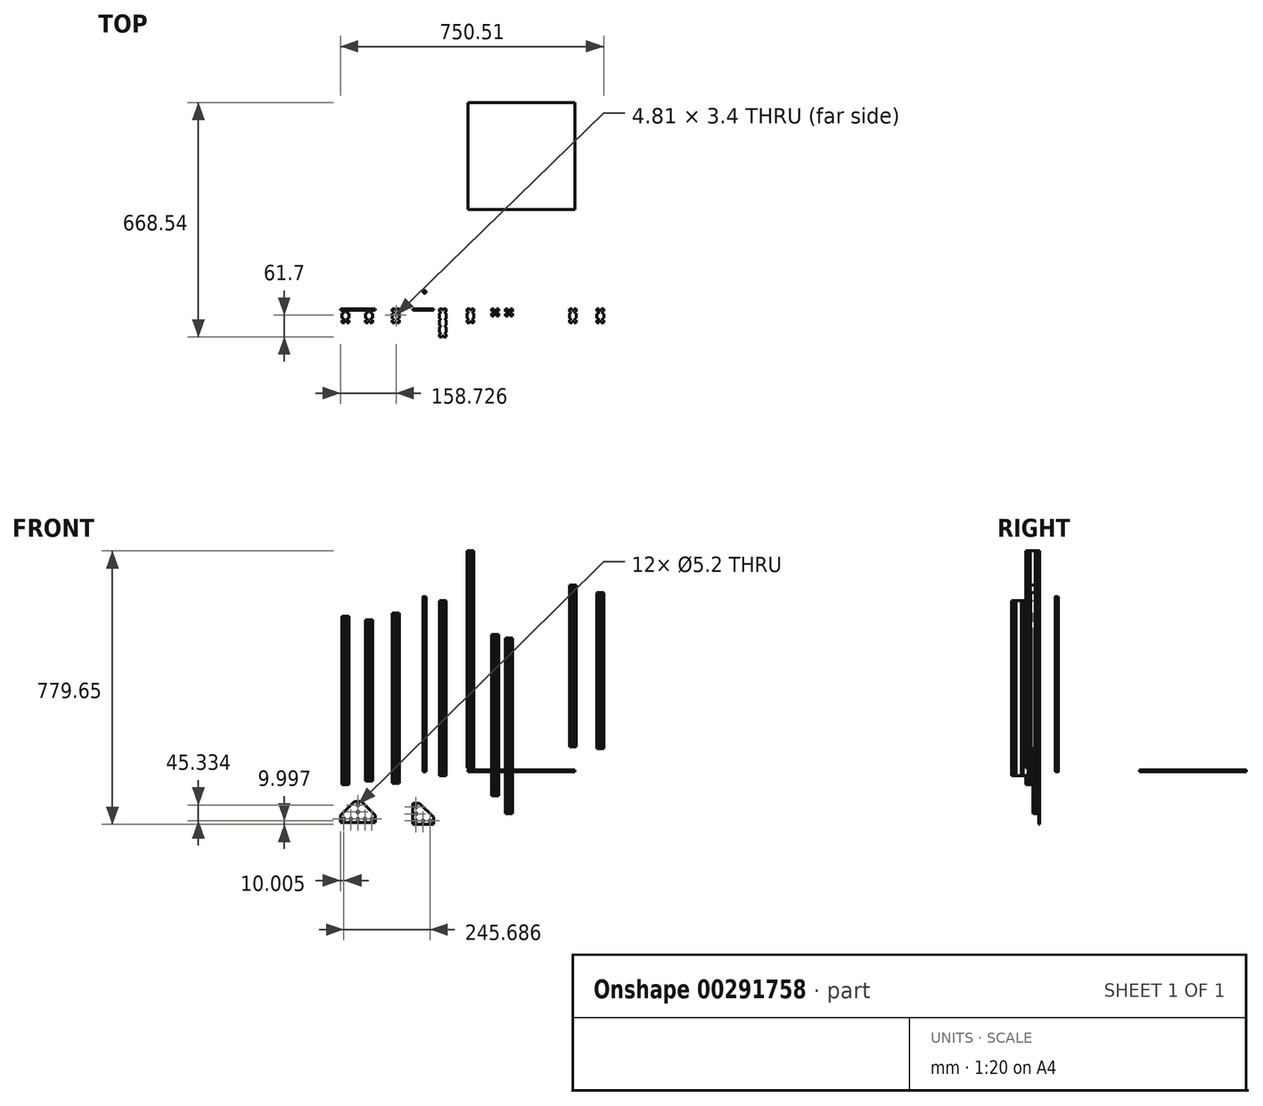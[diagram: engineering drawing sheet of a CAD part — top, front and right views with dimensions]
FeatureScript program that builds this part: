
annotation { "Feature Type Name" : "Feature", "Feature Type Description" : "" }
export const myFeature = defineFeature(function(context is Context, id is Id, definition is map)
    precondition{}
    {
        {
            var Q0;
            Q0=qCreatedBy(makeId("Front.planeOp"),FACE);
            var sketch = newSketch(context, id + "F0", { "sketchPlane" : qUnion([Q0])});
            skLineSegment(sketch, "E0.bottom", {"start": v(-21.8, 488.82) * mm, "end": v(-1.8, 488.82) * mm});
            skLineSegment(sketch, "E0.top", {"start": v(-21.8, -11.18) * mm, "end": v(-1.8, -11.18) * mm});
            skLineSegment(sketch, "E0.left", {"start": v(-21.8, 488.82) * mm, "end": v(-21.8, -11.18) * mm});
            skLineSegment(sketch, "E0.right", {"start": v(-1.8, 488.82) * mm, "end": v(-1.8, -11.18) * mm});
            skSolve(sketch);
        }
        {
            var Q0;
            Q0 = qSketchRegion(id + "F0", true);
            extrude(context, id + "F1", {"entities" : qUnion([Q0]), "depth" : 80 * mm});
        }
        {
            var Q0;
            Q0=qCreatedBy(makeId("Front.planeOp"),FACE);
            var sketch = newSketch(context, id + "F2", { "sketchPlane" : qUnion([Q0])});
            skLineSegment(sketch, "E1.bottom", {"start": v(56.98, 630.24) * mm, "end": v(76.98, 630.24) * mm});
            skLineSegment(sketch, "E1.top", {"start": v(56.98, 10.24) * mm, "end": v(76.98, 10.24) * mm});
            skLineSegment(sketch, "E1.left", {"start": v(56.98, 630.24) * mm, "end": v(56.98, 10.24) * mm});
            skLineSegment(sketch, "E1.right", {"start": v(76.98, 630.24) * mm, "end": v(76.98, 10.24) * mm});
            skSolve(sketch);
        }
        {
            var Q0;
            Q0 = qSketchRegion(id + "F2", true);
            extrude(context, id + "F3", {"entities" : qUnion([Q0]), "depth" : 40 * mm});
        }
        {
            var Q0;
            Q0=qCreatedBy(makeId("Front.planeOp"),FACE);
            var sketch = newSketch(context, id + "F4", { "sketchPlane" : qUnion([Q0])});
            skLineSegment(sketch, "E2.bottom", {"start": v(127.1, 391.51) * mm, "end": v(147.1, 391.51) * mm});
            skLineSegment(sketch, "E2.top", {"start": v(127.1, -68.49) * mm, "end": v(147.1, -68.49) * mm});
            skLineSegment(sketch, "E2.left", {"start": v(127.1, 391.51) * mm, "end": v(127.1, -68.49) * mm});
            skLineSegment(sketch, "E2.right", {"start": v(147.1, 391.51) * mm, "end": v(147.1, -68.49) * mm});
            skSolve(sketch);
        }
        {
            var Q0;
            Q0 = qSketchRegion(id + "F4", true);
            extrude(context, id + "F5", {"entities" : qUnion([Q0]), "depth" : 20 * mm});
        }
        {
            var Q0;
            Q0=qCreatedBy(makeId("Front.planeOp"),FACE);
            var sketch = newSketch(context, id + "F6", { "sketchPlane" : qUnion([Q0])});
            skLineSegment(sketch, "E3.bottom", {"start": v(349.08, 532.32) * mm, "end": v(369.08, 532.32) * mm});
            skLineSegment(sketch, "E3.top", {"start": v(349.08, 72.32) * mm, "end": v(369.08, 72.32) * mm});
            skLineSegment(sketch, "E3.left", {"start": v(349.08, 532.32) * mm, "end": v(349.08, 72.32) * mm});
            skLineSegment(sketch, "E3.right", {"start": v(369.08, 532.32) * mm, "end": v(369.08, 72.32) * mm});
            skSolve(sketch);
        }
        {
            var Q0;
            Q0 = qSketchRegion(id + "F6", true);
            extrude(context, id + "F7", {"entities" : qUnion([Q0]), "depth" : 40 * mm});
        }
        {
            var Q0;
            Q0=qCreatedBy(makeId("Front.planeOp"),FACE);
            var sketch = newSketch(context, id + "F8", { "sketchPlane" : qUnion([Q0])});
            skLineSegment(sketch, "E4.bottom", {"start": v(167.05, 381.28) * mm, "end": v(187.05, 381.28) * mm});
            skLineSegment(sketch, "E4.top", {"start": v(167.05, -118.72) * mm, "end": v(187.05, -118.72) * mm});
            skLineSegment(sketch, "E4.left", {"start": v(167.05, 381.28) * mm, "end": v(167.05, -118.72) * mm});
            skLineSegment(sketch, "E4.right", {"start": v(187.05, 381.28) * mm, "end": v(187.05, -118.72) * mm});
            skSolve(sketch);
        }
        {
            var Q0;
            Q0 = qSketchRegion(id + "F8", true);
            extrude(context, id + "F9", {"entities" : qUnion([Q0]), "depth" : 20 * mm});
        }
        {
            var Q0;
            Q0=qCreatedBy(makeId("Front.planeOp"),FACE);
            var sketch = newSketch(context, id + "F10", { "sketchPlane" : qUnion([Q0])});
            skLineSegment(sketch, "E5.bottom", {"start": v(-298.86, 444.23) * mm, "end": v(-278.86, 444.23) * mm});
            skLineSegment(sketch, "E5.top", {"start": v(-298.86, -35.77) * mm, "end": v(-278.86, -35.77) * mm});
            skLineSegment(sketch, "E5.left", {"start": v(-298.86, 444.23) * mm, "end": v(-298.86, -35.77) * mm});
            skLineSegment(sketch, "E5.right", {"start": v(-278.86, 444.23) * mm, "end": v(-278.86, -35.77) * mm});
            skSolve(sketch);
        }
        {
            var Q0;
            Q0 = qSketchRegion(id + "F10", true);
            extrude(context, id + "F11", {"entities" : qUnion([Q0]), "depth" : 40 * mm});
        }
        {
            var Q0;
            Q0=qCreatedBy(makeId("Front.planeOp"),FACE);
            var sketch = newSketch(context, id + "F12", { "sketchPlane" : qUnion([Q0])});
            skLineSegment(sketch, "E6.bottom", {"start": v(-232.38, 433.39) * mm, "end": v(-212.38, 433.39) * mm});
            skLineSegment(sketch, "E6.top", {"start": v(-232.38, -26.61) * mm, "end": v(-212.38, -26.61) * mm});
            skLineSegment(sketch, "E6.left", {"start": v(-232.38, 433.39) * mm, "end": v(-232.38, -26.61) * mm});
            skLineSegment(sketch, "E6.right", {"start": v(-212.38, 433.39) * mm, "end": v(-212.38, -26.61) * mm});
            skSolve(sketch);
        }
        {
            var Q0;
            Q0 = qSketchRegion(id + "F12", true);
            extrude(context, id + "F13", {"entities" : qUnion([Q0]), "depth" : 40 * mm});
        }
        {
            var Q0;
            Q0=qCreatedBy(makeId("Top.planeOp"),FACE);
            var sketch = newSketch(context, id + "F14", { "sketchPlane" : qUnion([Q0])});
            skCircle(sketch, "E7", {"center": v(-63.8, 48.43) * mm, "radius": 4 * mm});
            skSolve(sketch);
        }
        {
            var Q0;
            Q0 = qSketchRegion(id + "F14", true);
            extrude(context, id + "F15", {"entities" : qUnion([Q0]), "depth" : 500 * mm});
        }
        {
            var Q0;
            Q0=qCreatedBy(makeId("Top.planeOp"),FACE);
            var sketch = newSketch(context, id + "F16", { "sketchPlane" : qUnion([Q0])});
            skLineSegment(sketch, "E8.bottom", {"start": v(59.64, 588.54) * mm, "end": v(364.44, 588.54) * mm});
            skLineSegment(sketch, "E8.top", {"start": v(59.64, 283.74) * mm, "end": v(364.44, 283.74) * mm});
            skLineSegment(sketch, "E8.left", {"start": v(59.64, 588.54) * mm, "end": v(59.64, 283.74) * mm});
            skLineSegment(sketch, "E8.right", {"start": v(364.44, 588.54) * mm, "end": v(364.44, 283.74) * mm});
            skSolve(sketch);
        }
        {
            var Q0;
            Q0 = qSketchRegion(id + "F16", true);
            extrude(context, id + "F17", {"entities" : qUnion([Q0]), "depth" : 6 * mm});
        }
        {
            var Q0;
            Q0=qCreatedBy(makeId("Front.planeOp"),FACE);
            var sketch = newSketch(context, id + "F18", { "sketchPlane" : qUnion([Q0])});
            skLineSegment(sketch, "E9.bottom", {"start": v(-155.45, 452.3) * mm, "end": v(-135.45, 452.3) * mm});
            skLineSegment(sketch, "E9.top", {"start": v(-155.45, -32.7) * mm, "end": v(-135.45, -32.7) * mm});
            skLineSegment(sketch, "E9.left", {"start": v(-155.45, 452.3) * mm, "end": v(-155.45, -32.7) * mm});
            skLineSegment(sketch, "E9.right", {"start": v(-135.45, 452.3) * mm, "end": v(-135.45, -32.7) * mm});
            skSolve(sketch);
        }
        {
            var Q0;
            Q0 = qSketchRegion(id + "F18", true);
            extrude(context, id + "F19", {"entities" : qUnion([Q0]), "depth" : 40 * mm});
        }
        {
            var Q0;
            Q0=qCreatedBy(makeId("Front.planeOp"),FACE);
            var sketch = newSketch(context, id + "F20", { "sketchPlane" : qUnion([Q0])});
            skLineSegment(sketch, "E10.bottom", {"start": v(426.75, 511.38) * mm, "end": v(446.75, 511.38) * mm});
            skLineSegment(sketch, "E10.top", {"start": v(426.75, 66.38) * mm, "end": v(446.75, 66.38) * mm});
            skLineSegment(sketch, "E10.left", {"start": v(426.75, 511.38) * mm, "end": v(426.75, 66.38) * mm});
            skLineSegment(sketch, "E10.right", {"start": v(446.75, 511.38) * mm, "end": v(446.75, 66.38) * mm});
            skSolve(sketch);
        }
        {
            var Q0;
            Q0 = qSketchRegion(id + "F20", true);
            extrude(context, id + "F21", {"entities" : qUnion([Q0]), "depth" : 40 * mm});
        }
        {
            var Q0;
            Q0=makeQuery(id+"F11.opExtrude","SWEPT_FACE",FACE,{"disambiguationData":[OSD([sQuery(id+"F10.wireOp",EDGE,"E5.bottom")])]});
            var sketch = newSketch(context, id + "F22", { "sketchPlane" : qUnion([Q0])});
            skLineSegment(sketch, "E11", {"start": v(-288.86, 0) * mm, "end": v(-288.86, -40) * mm, "construction": true});
            skLineSegment(sketch, "E12", {"start": v(-288.86, -40) * mm, "end": v(-298.86, -20) * mm, "construction": true});
            skLineSegment(sketch, "E13", {"start": v(-298.86, -20) * mm, "end": v(-278.86, 0) * mm, "construction": true});
            skLineSegment(sketch, "E14", {"start": v(-288.86, -10) * mm, "end": v(-283.86, -10) * mm, "construction": true});
            skPoint(sketch, "E15.oppositeSnap0", {"position": v(-283.86, -10) * mm});
            skLineSegment(sketch, "E15.top", {"start": v(-278.86, -6.61) * mm, "end": v(-283.86, -6.61) * mm});
            skLineSegment(sketch, "E15.left", {"start": v(-278.86, -10) * mm, "end": v(-278.86, -6.61) * mm});
            skLineSegment(sketch, "E15.right", {"start": v(-283.86, -10) * mm, "end": v(-283.86, -6.61) * mm});
            skLineSegment(sketch, "E16.MirrorCS", {"start": v(-278.86, -13.39) * mm, "end": v(-283.86, -13.39) * mm});
            skLineSegment(sketch, "E17.MirrorCS", {"start": v(-283.86, -10) * mm, "end": v(-283.86, -13.39) * mm});
            skLineSegment(sketch, "E18.MirrorCS", {"start": v(-278.86, -10) * mm, "end": v(-278.86, -13.39) * mm});
            skLineSegment(sketch, "E19", {"start": v(-298.86, -20) * mm, "end": v(-278.86, -20) * mm, "construction": true});
            skLineSegment(sketch, "E20.MirrorCS", {"start": v(-278.86, -26.61) * mm, "end": v(-283.86, -26.61) * mm});
            skLineSegment(sketch, "E21.MirrorCS", {"start": v(-283.86, -30) * mm, "end": v(-283.86, -26.61) * mm});
            skLineSegment(sketch, "E22.MirrorCS", {"start": v(-283.86, -30) * mm, "end": v(-283.86, -33.39) * mm});
            skLineSegment(sketch, "E23.MirrorCS", {"start": v(-278.86, -33.39) * mm, "end": v(-283.86, -33.39) * mm});
            skLineSegment(sketch, "E24.MirrorCS", {"start": v(-278.86, -30) * mm, "end": v(-278.86, -33.39) * mm});
            skLineSegment(sketch, "E25.MirrorCS", {"start": v(-278.86, -30) * mm, "end": v(-278.86, -26.61) * mm});
            skLineSegment(sketch, "E26.MirrorCS", {"start": v(-298.86, -13.39) * mm, "end": v(-293.86, -13.39) * mm});
            skLineSegment(sketch, "E27.MirrorCS", {"start": v(-298.86, -6.61) * mm, "end": v(-293.86, -6.61) * mm});
            skLineSegment(sketch, "E28.MirrorCS", {"start": v(-293.86, -10) * mm, "end": v(-293.86, -6.61) * mm});
            skLineSegment(sketch, "E29.MirrorCS", {"start": v(-293.86, -10) * mm, "end": v(-293.86, -13.39) * mm});
            skLineSegment(sketch, "E30.MirrorCS", {"start": v(-298.86, -26.61) * mm, "end": v(-293.86, -26.61) * mm});
            skLineSegment(sketch, "E31.MirrorCS", {"start": v(-293.86, -30) * mm, "end": v(-293.86, -26.61) * mm});
            skLineSegment(sketch, "E32.MirrorCS", {"start": v(-298.86, -33.39) * mm, "end": v(-293.86, -33.39) * mm});
            skLineSegment(sketch, "E33.MirrorCS", {"start": v(-293.86, -30) * mm, "end": v(-293.86, -33.39) * mm});
            skLineSegment(sketch, "E34.MirrorCS", {"start": v(-298.86, -30) * mm, "end": v(-298.86, -33.39) * mm});
            skLineSegment(sketch, "E35.MirrorCS", {"start": v(-298.86, -30) * mm, "end": v(-298.86, -26.61) * mm});
            skLineSegment(sketch, "E36.MirrorCS", {"start": v(-298.86, -10) * mm, "end": v(-298.86, -13.39) * mm});
            skLineSegment(sketch, "E37.MirrorCS", {"start": v(-298.86, -10) * mm, "end": v(-298.86, -6.61) * mm});
            skLineSegment(sketch, "E38.MirrorCS", {"start": v(-285.47, 0) * mm, "end": v(-285.47, -5) * mm});
            skLineSegment(sketch, "E39.MirrorCS", {"start": v(-292.25, 0) * mm, "end": v(-292.25, -5) * mm});
            skLineSegment(sketch, "E40.MirrorCS", {"start": v(-288.86, -5) * mm, "end": v(-285.47, -5) * mm});
            skLineSegment(sketch, "E41.MirrorCS", {"start": v(-288.86, -5) * mm, "end": v(-292.25, -5) * mm});
            skLineSegment(sketch, "E42.MirrorCS", {"start": v(-288.86, 0) * mm, "end": v(-292.25, 0) * mm});
            skLineSegment(sketch, "E43.MirrorCS", {"start": v(-288.86, 0) * mm, "end": v(-285.47, 0) * mm});
            skLineSegment(sketch, "E44.MirrorCS", {"start": v(-288.86, -35) * mm, "end": v(-292.25, -35) * mm});
            skLineSegment(sketch, "E45.MirrorCS", {"start": v(-292.25, -40) * mm, "end": v(-292.25, -35) * mm});
            skLineSegment(sketch, "E46.MirrorCS", {"start": v(-285.47, -40) * mm, "end": v(-285.47, -35) * mm});
            skLineSegment(sketch, "E47.MirrorCS", {"start": v(-288.86, -35) * mm, "end": v(-285.47, -35) * mm});
            skLineSegment(sketch, "E48.MirrorCS", {"start": v(-288.86, -40) * mm, "end": v(-285.47, -40) * mm});
            skLineSegment(sketch, "E49.MirrorCS", {"start": v(-288.86, -40) * mm, "end": v(-292.25, -40) * mm});
            skSolve(sketch);
        }
        {
            var Q0;
            Q0 = qSketchRegion(id + "F22", true);
            extrude(context, id + "F23", {"entities" : qUnion([Q0]), "operationType" : NewBodyOperationType.REMOVE, "oppositeDirection" : true, "depth" : 900 * mm});
        }
        {
            var Q0;
            Q0=makeQuery(id+"F1.opExtrude","SWEPT_FACE",FACE,{"disambiguationData":[OSD([sQuery(id+"F0.wireOp",EDGE,"E0.bottom")])]});
            var sketch = newSketch(context, id + "F24", { "sketchPlane" : qUnion([Q0])});
            skLineSegment(sketch, "E50", {"start": v(-21.8, -40) * mm, "end": v(-1.8, -40) * mm, "construction": true});
            skLineSegment(sketch, "E51", {"start": v(-1.8, -40) * mm, "end": v(-11.8, 0) * mm, "construction": true});
            skLineSegment(sketch, "E52", {"start": v(-11.8, 0) * mm, "end": v(-11.8, -80) * mm, "construction": true});
            skLineSegment(sketch, "E53", {"start": v(-21.8, -80) * mm, "end": v(-1.8, -40) * mm, "construction": true});
            skLineSegment(sketch, "E54", {"start": v(-21.8, -40) * mm, "end": v(-1.8, 0) * mm, "construction": true});
            skLineSegment(sketch, "E55", {"start": v(-11.8, -20) * mm, "end": v(-1.8, -20) * mm, "construction": true});
            skLineSegment(sketch, "E56", {"start": v(-11.8, -20) * mm, "end": v(-1.8, -40) * mm, "construction": true});
            skLineSegment(sketch, "E57", {"start": v(-11.8, -40) * mm, "end": v(-1.8, -20) * mm, "construction": true});
            skLineSegment(sketch, "E58", {"start": v(-6.8, -30) * mm, "end": v(-1.8, -30) * mm, "construction": true});
            skLineSegment(sketch, "E59.bottom", {"start": v(-4.87, -27.72) * mm, "end": v(-1.8, -27.72) * mm});
            skLineSegment(sketch, "E59.top", {"start": v(-4.87, -32.4) * mm, "end": v(-1.8, -32.4) * mm});
            skLineSegment(sketch, "E59.left", {"start": v(-4.87, -27.72) * mm, "end": v(-4.87, -32.4) * mm});
            skLineSegment(sketch, "E59.right", {"start": v(-1.8, -27.72) * mm, "end": v(-1.8, -32.4) * mm});
            skLineSegment(sketch, "E60.MirrorCS", {"start": v(-4.87, -12.28) * mm, "end": v(-1.8, -12.28) * mm});
            skLineSegment(sketch, "E61.MirrorCS", {"start": v(-4.87, -12.28) * mm, "end": v(-4.87, -7.6) * mm});
            skLineSegment(sketch, "E62.MirrorCS", {"start": v(-4.87, -7.6) * mm, "end": v(-1.8, -7.6) * mm});
            skLineSegment(sketch, "E63.MirrorCS", {"start": v(-1.8, -12.28) * mm, "end": v(-1.8, -7.6) * mm});
            skLineSegment(sketch, "E64.MirrorCS", {"start": v(-18.73, -12.28) * mm, "end": v(-21.8, -12.28) * mm});
            skLineSegment(sketch, "E65.MirrorCS", {"start": v(-18.73, -12.28) * mm, "end": v(-18.73, -7.6) * mm});
            skLineSegment(sketch, "E66.MirrorCS", {"start": v(-18.73, -7.6) * mm, "end": v(-21.8, -7.6) * mm});
            skLineSegment(sketch, "E67.MirrorCS", {"start": v(-21.8, -12.28) * mm, "end": v(-21.8, -7.6) * mm});
            skLineSegment(sketch, "E68.MirrorCS", {"start": v(-18.73, -27.72) * mm, "end": v(-21.8, -27.72) * mm});
            skLineSegment(sketch, "E69.MirrorCS", {"start": v(-18.73, -27.72) * mm, "end": v(-18.73, -32.4) * mm});
            skLineSegment(sketch, "E70.MirrorCS", {"start": v(-21.8, -40) * mm, "end": v(-11.8, 0) * mm, "construction": true});
            skLineSegment(sketch, "E71.MirrorCS", {"start": v(-18.73, -32.4) * mm, "end": v(-21.8, -32.4) * mm});
            skLineSegment(sketch, "E72.MirrorCS", {"start": v(-21.8, -27.72) * mm, "end": v(-21.8, -32.4) * mm});
            skLineSegment(sketch, "E73.bottom", {"start": v(-14.19, 0) * mm, "end": v(-9.32, 0) * mm});
            skLineSegment(sketch, "E73.top", {"start": v(-14.19, -3.05) * mm, "end": v(-9.32, -3.05) * mm});
            skLineSegment(sketch, "E73.left", {"start": v(-14.19, 0) * mm, "end": v(-14.19, -3.05) * mm});
            skLineSegment(sketch, "E73.right", {"start": v(-9.32, 0) * mm, "end": v(-9.32, -3.05) * mm});
            skLineSegment(sketch, "E74.MirrorCS", {"start": v(-14.19, -80) * mm, "end": v(-9.32, -80) * mm});
            skLineSegment(sketch, "E75.MirrorCS", {"start": v(-1.8, -52.28) * mm, "end": v(-1.8, -47.6) * mm});
            skLineSegment(sketch, "E76.MirrorCS", {"start": v(-18.73, -67.72) * mm, "end": v(-21.8, -67.72) * mm});
            skLineSegment(sketch, "E77.MirrorCS", {"start": v(-18.73, -67.72) * mm, "end": v(-18.73, -72.4) * mm});
            skLineSegment(sketch, "E78.MirrorCS", {"start": v(-4.87, -52.28) * mm, "end": v(-4.87, -47.6) * mm});
            skLineSegment(sketch, "E79.MirrorCS", {"start": v(-14.19, -76.95) * mm, "end": v(-9.32, -76.95) * mm});
            skLineSegment(sketch, "E80.MirrorCS", {"start": v(-4.87, -52.28) * mm, "end": v(-1.8, -52.28) * mm});
            skLineSegment(sketch, "E81.MirrorCS", {"start": v(-14.19, -80) * mm, "end": v(-14.19, -76.95) * mm});
            skLineSegment(sketch, "E82.MirrorCS", {"start": v(-1.8, -67.72) * mm, "end": v(-1.8, -72.4) * mm});
            skLineSegment(sketch, "E83.MirrorCS", {"start": v(-9.32, -80) * mm, "end": v(-9.32, -76.95) * mm});
            skLineSegment(sketch, "E84.MirrorCS", {"start": v(-18.73, -47.6) * mm, "end": v(-21.8, -47.6) * mm});
            skLineSegment(sketch, "E85.MirrorCS", {"start": v(-4.87, -67.72) * mm, "end": v(-4.87, -72.4) * mm});
            skLineSegment(sketch, "E86.MirrorCS", {"start": v(-4.87, -47.6) * mm, "end": v(-1.8, -47.6) * mm});
            skLineSegment(sketch, "E87.MirrorCS", {"start": v(-18.73, -72.4) * mm, "end": v(-21.8, -72.4) * mm});
            skLineSegment(sketch, "E88.MirrorCS", {"start": v(-11.8, -60) * mm, "end": v(-1.8, -60) * mm, "construction": true});
            skLineSegment(sketch, "E89.MirrorCS", {"start": v(-6.8, -50) * mm, "end": v(-1.8, -50) * mm, "construction": true});
            skLineSegment(sketch, "E90.MirrorCS", {"start": v(-21.8, -67.72) * mm, "end": v(-21.8, -72.4) * mm});
            skLineSegment(sketch, "E91.MirrorCS", {"start": v(-18.73, -52.28) * mm, "end": v(-21.8, -52.28) * mm});
            skLineSegment(sketch, "E92.MirrorCS", {"start": v(-21.8, -52.28) * mm, "end": v(-21.8, -47.6) * mm});
            skLineSegment(sketch, "E93.MirrorCS", {"start": v(-4.87, -72.4) * mm, "end": v(-1.8, -72.4) * mm});
            skLineSegment(sketch, "E94.MirrorCS", {"start": v(-18.73, -52.28) * mm, "end": v(-18.73, -47.6) * mm});
            skLineSegment(sketch, "E95.MirrorCS", {"start": v(-4.87, -67.72) * mm, "end": v(-1.8, -67.72) * mm});
            skSolve(sketch);
        }
        {
            var Q0;
            Q0 = qSketchRegion(id + "F24", true);
            extrude(context, id + "F25", {"entities" : qUnion([Q0]), "operationType" : NewBodyOperationType.REMOVE, "oppositeDirection" : true, "depth" : 999 * mm});
        }
        {
            var Q0;
            Q0=makeQuery(id+"F3.opExtrude","SWEPT_FACE",FACE,{"disambiguationData":[OSD([sQuery(id+"F2.wireOp",EDGE,"E1.bottom")])]});
            var sketch = newSketch(context, id + "F26", { "sketchPlane" : qUnion([Q0])});
            skLineSegment(sketch, "E96", {"start": v(66.98, 0) * mm, "end": v(66.98, -40) * mm, "construction": true});
            skLineSegment(sketch, "E97", {"start": v(56.98, -20) * mm, "end": v(76.98, -20) * mm, "construction": true});
            skLineSegment(sketch, "E98", {"start": v(76.98, -20) * mm, "end": v(56.98, 0) * mm, "construction": true});
            skLineSegment(sketch, "E99", {"start": v(66.98, -10) * mm, "end": v(76.98, -10) * mm, "construction": true});
            skLineSegment(sketch, "E100.bottom", {"start": v(76.98, -7.44) * mm, "end": v(73.45, -7.44) * mm});
            skLineSegment(sketch, "E100.top", {"start": v(76.98, -12.74) * mm, "end": v(73.45, -12.74) * mm});
            skLineSegment(sketch, "E100.left", {"start": v(76.98, -7.44) * mm, "end": v(76.98, -12.74) * mm});
            skLineSegment(sketch, "E100.right", {"start": v(73.45, -7.44) * mm, "end": v(73.45, -12.74) * mm});
            skLineSegment(sketch, "E101.bottom", {"start": v(64.57, 0) * mm, "end": v(69.67, 0) * mm});
            skLineSegment(sketch, "E101.top", {"start": v(64.57, -3.15) * mm, "end": v(69.67, -3.15) * mm});
            skLineSegment(sketch, "E101.left", {"start": v(64.57, 0) * mm, "end": v(64.57, -3.15) * mm});
            skLineSegment(sketch, "E101.right", {"start": v(69.67, 0) * mm, "end": v(69.67, -3.15) * mm});
            skLineSegment(sketch, "E102.MirrorCS", {"start": v(56.98, -12.74) * mm, "end": v(60.52, -12.74) * mm});
            skLineSegment(sketch, "E103.MirrorCS", {"start": v(56.98, -7.44) * mm, "end": v(60.52, -7.44) * mm});
            skLineSegment(sketch, "E104.MirrorCS", {"start": v(60.52, -7.44) * mm, "end": v(60.52, -12.74) * mm});
            skLineSegment(sketch, "E105.MirrorCS", {"start": v(56.98, -7.44) * mm, "end": v(56.98, -12.74) * mm});
            skLineSegment(sketch, "E106.MirrorCS", {"start": v(56.98, -7.26) * mm, "end": v(60.52, -7.26) * mm});
            skLineSegment(sketch, "E107.MirrorCS", {"start": v(56.98, -12.56) * mm, "end": v(60.52, -12.56) * mm});
            skLineSegment(sketch, "E108.MirrorCS", {"start": v(60.52, -12.56) * mm, "end": v(60.52, -7.26) * mm});
            skLineSegment(sketch, "E109.MirrorCS", {"start": v(56.98, -12.56) * mm, "end": v(56.98, -7.26) * mm});
            skLineSegment(sketch, "E110.MirrorCS", {"start": v(76.98, -12.56) * mm, "end": v(73.45, -12.56) * mm});
            skLineSegment(sketch, "E111.MirrorCS", {"start": v(73.45, -12.56) * mm, "end": v(73.45, -7.26) * mm});
            skLineSegment(sketch, "E112.MirrorCS", {"start": v(76.98, -7.26) * mm, "end": v(73.45, -7.26) * mm});
            skLineSegment(sketch, "E113.MirrorCS", {"start": v(76.98, -12.56) * mm, "end": v(76.98, -7.26) * mm});
            skLineSegment(sketch, "E114.MirrorCS", {"start": v(56.98, 0) * mm, "end": v(76.98, 0) * mm, "construction": true});
            skLineSegment(sketch, "E115.MirrorCS", {"start": v(76.98, 0) * mm, "end": v(56.98, -20) * mm, "construction": true});
            skLineSegment(sketch, "E116.MirrorCS", {"start": v(76.98, -27.44) * mm, "end": v(76.98, -32.74) * mm});
            skLineSegment(sketch, "E117.MirrorCS", {"start": v(56.98, -32.56) * mm, "end": v(56.98, -27.26) * mm});
            skLineSegment(sketch, "E118.MirrorCS", {"start": v(76.98, -32.56) * mm, "end": v(76.98, -27.26) * mm});
            skLineSegment(sketch, "E119.MirrorCS", {"start": v(73.45, -27.44) * mm, "end": v(73.45, -32.74) * mm});
            skLineSegment(sketch, "E120.MirrorCS", {"start": v(60.52, -32.56) * mm, "end": v(60.52, -27.26) * mm});
            skLineSegment(sketch, "E121.MirrorCS", {"start": v(56.98, -27.44) * mm, "end": v(56.98, -32.74) * mm});
            skLineSegment(sketch, "E122.MirrorCS", {"start": v(64.57, -40) * mm, "end": v(69.67, -40) * mm});
            skLineSegment(sketch, "E123.MirrorCS", {"start": v(73.45, -32.56) * mm, "end": v(73.45, -27.26) * mm});
            skLineSegment(sketch, "E124.MirrorCS", {"start": v(60.52, -27.44) * mm, "end": v(60.52, -32.74) * mm});
            skLineSegment(sketch, "E125.MirrorCS", {"start": v(76.98, -32.74) * mm, "end": v(73.45, -32.74) * mm});
            skLineSegment(sketch, "E126.MirrorCS", {"start": v(56.98, -32.74) * mm, "end": v(60.52, -32.74) * mm});
            skLineSegment(sketch, "E127.MirrorCS", {"start": v(56.98, -27.44) * mm, "end": v(60.52, -27.44) * mm});
            skLineSegment(sketch, "E128.MirrorCS", {"start": v(64.57, -40) * mm, "end": v(64.57, -36.85) * mm});
            skLineSegment(sketch, "E129.MirrorCS", {"start": v(69.67, -40) * mm, "end": v(69.67, -36.85) * mm});
            skLineSegment(sketch, "E130.MirrorCS", {"start": v(56.98, -27.26) * mm, "end": v(60.52, -27.26) * mm});
            skLineSegment(sketch, "E131.MirrorCS", {"start": v(76.98, -32.56) * mm, "end": v(73.45, -32.56) * mm});
            skLineSegment(sketch, "E132.MirrorCS", {"start": v(76.98, -27.44) * mm, "end": v(73.45, -27.44) * mm});
            skLineSegment(sketch, "E133.MirrorCS", {"start": v(56.98, -32.56) * mm, "end": v(60.52, -32.56) * mm});
            skLineSegment(sketch, "E134.MirrorCS", {"start": v(76.98, -27.26) * mm, "end": v(73.45, -27.26) * mm});
            skLineSegment(sketch, "E135.MirrorCS", {"start": v(64.57, -36.85) * mm, "end": v(69.67, -36.85) * mm});
            skLineSegment(sketch, "E136.MirrorCS", {"start": v(56.98, -40) * mm, "end": v(76.98, -40) * mm, "construction": true});
            skLineSegment(sketch, "E137.MirrorCS", {"start": v(66.98, -30) * mm, "end": v(76.98, -30) * mm, "construction": true});
            skSolve(sketch);
        }
        {
            var Q0;
            Q0 = qSketchRegion(id + "F26", true);
            extrude(context, id + "F27", {"entities" : qUnion([Q0]), "operationType" : NewBodyOperationType.REMOVE, "oppositeDirection" : true, "depth" : 999 * mm});
        }
        {
            var Q0;
            Q0=makeQuery(id+"F19.opExtrude","SWEPT_FACE",FACE,{"disambiguationData":[OSD([sQuery(id+"F18.wireOp",EDGE,"E9.bottom")])]});
            var sketch = newSketch(context, id + "F28", { "sketchPlane" : qUnion([Q0])});
            skLineSegment(sketch, "E138", {"start": v(-155.45, -20) * mm, "end": v(-135.45, -20) * mm, "construction": true});
            skLineSegment(sketch, "E139", {"start": v(-135.45, -20) * mm, "end": v(-155.45, 0) * mm, "construction": true});
            skLineSegment(sketch, "E140.bottom", {"start": v(-147.9, 0) * mm, "end": v(-142.97, 0) * mm});
            skLineSegment(sketch, "E140.top", {"start": v(-147.9, -2.85) * mm, "end": v(-142.97, -2.85) * mm});
            skLineSegment(sketch, "E140.left", {"start": v(-147.9, 0) * mm, "end": v(-147.9, -2.85) * mm});
            skLineSegment(sketch, "E140.right", {"start": v(-142.97, 0) * mm, "end": v(-142.97, -2.85) * mm});
            skLineSegment(sketch, "E141.bottom", {"start": v(-135.45, -8) * mm, "end": v(-138.85, -8) * mm});
            skLineSegment(sketch, "E141.top", {"start": v(-135.45, -12.82) * mm, "end": v(-138.85, -12.82) * mm});
            skLineSegment(sketch, "E141.left", {"start": v(-135.45, -8) * mm, "end": v(-135.45, -12.82) * mm});
            skLineSegment(sketch, "E141.right", {"start": v(-138.85, -8) * mm, "end": v(-138.85, -12.82) * mm});
            skLineSegment(sketch, "E142.MirrorCS", {"start": v(-152.6, -7.55) * mm, "end": v(-152.6, -12.48) * mm});
            skLineSegment(sketch, "E143.MirrorCS", {"start": v(-147.44, -20) * mm, "end": v(-142.63, -20) * mm});
            skLineSegment(sketch, "E144.MirrorCS", {"start": v(-142.63, -20) * mm, "end": v(-142.63, -16.6) * mm});
            skLineSegment(sketch, "E145.MirrorCS", {"start": v(-147.44, -16.6) * mm, "end": v(-142.63, -16.6) * mm});
            skLineSegment(sketch, "E146.MirrorCS", {"start": v(-155.45, -7.55) * mm, "end": v(-152.6, -7.55) * mm});
            skLineSegment(sketch, "E147.MirrorCS", {"start": v(-155.45, -12.48) * mm, "end": v(-152.6, -12.48) * mm});
            skLineSegment(sketch, "E148.MirrorCS", {"start": v(-155.45, -7.55) * mm, "end": v(-155.45, -12.48) * mm});
            skLineSegment(sketch, "E149.MirrorCS", {"start": v(-147.44, -20) * mm, "end": v(-147.44, -16.6) * mm});
            skLineSegment(sketch, "E150.MirrorCS", {"start": v(-142.97, -40) * mm, "end": v(-142.97, -37.15) * mm});
            skLineSegment(sketch, "E151.MirrorCS", {"start": v(-147.9, -40) * mm, "end": v(-147.9, -37.15) * mm});
            skLineSegment(sketch, "E152.MirrorCS", {"start": v(-155.45, -27.52) * mm, "end": v(-152.6, -27.52) * mm});
            skLineSegment(sketch, "E153.MirrorCS", {"start": v(-155.45, -32.45) * mm, "end": v(-152.6, -32.45) * mm});
            skLineSegment(sketch, "E154.MirrorCS", {"start": v(-152.6, -32.45) * mm, "end": v(-152.6, -27.52) * mm});
            skLineSegment(sketch, "E155.MirrorCS", {"start": v(-138.85, -32) * mm, "end": v(-138.85, -27.18) * mm});
            skLineSegment(sketch, "E156.MirrorCS", {"start": v(-135.45, -32) * mm, "end": v(-135.45, -27.18) * mm});
            skLineSegment(sketch, "E157.MirrorCS", {"start": v(-147.9, -40) * mm, "end": v(-142.97, -40) * mm});
            skLineSegment(sketch, "E158.MirrorCS", {"start": v(-155.45, -32.45) * mm, "end": v(-155.45, -27.52) * mm});
            skLineSegment(sketch, "E159.MirrorCS", {"start": v(-135.45, -27.18) * mm, "end": v(-138.85, -27.18) * mm});
            skLineSegment(sketch, "E160.MirrorCS", {"start": v(-135.45, -32) * mm, "end": v(-138.85, -32) * mm});
            skLineSegment(sketch, "E161.MirrorCS", {"start": v(-147.9, -37.15) * mm, "end": v(-142.97, -37.15) * mm});
            skSolve(sketch);
        }
        {
            var Q0;
            Q0 = qSketchRegion(id + "F28", true);
            extrude(context, id + "F29", {"entities" : qUnion([Q0]), "operationType" : NewBodyOperationType.REMOVE, "oppositeDirection" : true, "depth" : 999 * mm});
        }
        {
            var Q0;
            Q0=makeQuery(id+"F13.opExtrude","SWEPT_FACE",FACE,{"disambiguationData":[OSD([sQuery(id+"F12.wireOp",EDGE,"E6.bottom")])]});
            var sketch = newSketch(context, id + "F30", { "sketchPlane" : qUnion([Q0])});
            skLineSegment(sketch, "E162.bottom", {"start": v(-224.59, 0) * mm, "end": v(-220, 0) * mm});
            skLineSegment(sketch, "E162.top", {"start": v(-224.59, -4.54) * mm, "end": v(-220, -4.54) * mm});
            skLineSegment(sketch, "E162.left", {"start": v(-224.59, 0) * mm, "end": v(-224.59, -4.54) * mm});
            skLineSegment(sketch, "E162.right", {"start": v(-220, 0) * mm, "end": v(-220, -4.54) * mm});
            skLineSegment(sketch, "E163.bottom", {"start": v(-212.38, -8.2) * mm, "end": v(-217.51, -8.2) * mm});
            skLineSegment(sketch, "E163.top", {"start": v(-212.38, -12.66) * mm, "end": v(-217.51, -12.66) * mm});
            skLineSegment(sketch, "E163.left", {"start": v(-212.38, -8.2) * mm, "end": v(-212.38, -12.66) * mm});
            skLineSegment(sketch, "E163.right", {"start": v(-217.51, -8.2) * mm, "end": v(-217.51, -12.66) * mm});
            skLineSegment(sketch, "E164.bottom", {"start": v(-232.38, -8.2) * mm, "end": v(-227.47, -8.2) * mm});
            skLineSegment(sketch, "E164.top", {"start": v(-232.38, -12.66) * mm, "end": v(-227.47, -12.66) * mm});
            skLineSegment(sketch, "E164.left", {"start": v(-232.38, -8.2) * mm, "end": v(-232.38, -12.66) * mm});
            skLineSegment(sketch, "E164.right", {"start": v(-227.47, -8.2) * mm, "end": v(-227.47, -12.66) * mm});
            skLineSegment(sketch, "E165", {"start": v(-232.38, -20) * mm, "end": v(-212.38, -20) * mm, "construction": true});
            skLineSegment(sketch, "E166.MirrorCS", {"start": v(-217.51, -31.8) * mm, "end": v(-217.51, -27.34) * mm});
            skLineSegment(sketch, "E167.MirrorCS", {"start": v(-220, -40) * mm, "end": v(-220, -35.46) * mm});
            skLineSegment(sketch, "E168.MirrorCS", {"start": v(-212.38, -31.8) * mm, "end": v(-217.51, -31.8) * mm});
            skLineSegment(sketch, "E169.MirrorCS", {"start": v(-232.38, -31.8) * mm, "end": v(-227.47, -31.8) * mm});
            skLineSegment(sketch, "E170.MirrorCS", {"start": v(-212.38, -27.34) * mm, "end": v(-217.51, -27.34) * mm});
            skLineSegment(sketch, "E171.MirrorCS", {"start": v(-224.59, -40) * mm, "end": v(-220, -40) * mm});
            skLineSegment(sketch, "E172.MirrorCS", {"start": v(-232.38, -27.34) * mm, "end": v(-227.47, -27.34) * mm});
            skLineSegment(sketch, "E173.MirrorCS", {"start": v(-212.38, -31.8) * mm, "end": v(-212.38, -27.34) * mm});
            skLineSegment(sketch, "E174.MirrorCS", {"start": v(-232.38, -31.8) * mm, "end": v(-232.38, -27.34) * mm});
            skLineSegment(sketch, "E175.MirrorCS", {"start": v(-227.47, -31.8) * mm, "end": v(-227.47, -27.34) * mm});
            skLineSegment(sketch, "E176.MirrorCS", {"start": v(-224.59, -35.46) * mm, "end": v(-220, -35.46) * mm});
            skLineSegment(sketch, "E177.MirrorCS", {"start": v(-224.59, -40) * mm, "end": v(-224.59, -35.46) * mm});
            skSolve(sketch);
        }
        {
            var Q0;
            Q0 = qSketchRegion(id + "F30", true);
            extrude(context, id + "F31", {"entities" : qUnion([Q0]), "operationType" : NewBodyOperationType.REMOVE, "oppositeDirection" : true, "depth" : 999 * mm});
        }
        {
            var Q0;
            Q0=makeQuery(id+"F5.opExtrude","SWEPT_FACE",FACE,{"disambiguationData":[OSD([sQuery(id+"F4.wireOp",EDGE,"E2.bottom")])]});
            var sketch = newSketch(context, id + "F32", { "sketchPlane" : qUnion([Q0])});
            skLineSegment(sketch, "E178.bottom", {"start": v(133.68, 0) * mm, "end": v(140.63, 0) * mm});
            skLineSegment(sketch, "E178.top", {"start": v(133.68, -4.88) * mm, "end": v(140.63, -4.88) * mm});
            skLineSegment(sketch, "E178.left", {"start": v(133.68, 0) * mm, "end": v(133.68, -4.88) * mm});
            skLineSegment(sketch, "E178.right", {"start": v(140.63, 0) * mm, "end": v(140.63, -4.88) * mm});
            skLineSegment(sketch, "E179.bottom", {"start": v(147.1, -6.75) * mm, "end": v(142.9, -6.75) * mm});
            skLineSegment(sketch, "E179.top", {"start": v(147.1, -12.9) * mm, "end": v(142.9, -12.9) * mm});
            skLineSegment(sketch, "E179.left", {"start": v(147.1, -6.75) * mm, "end": v(147.1, -12.9) * mm});
            skLineSegment(sketch, "E179.right", {"start": v(142.9, -6.75) * mm, "end": v(142.9, -12.9) * mm});
            skLineSegment(sketch, "E180.bottom", {"start": v(140.63, -20) * mm, "end": v(133.68, -20) * mm});
            skLineSegment(sketch, "E180.top", {"start": v(140.63, -14.5) * mm, "end": v(133.68, -14.5) * mm});
            skLineSegment(sketch, "E180.left", {"start": v(140.63, -20) * mm, "end": v(140.63, -14.5) * mm});
            skLineSegment(sketch, "E180.right", {"start": v(133.68, -20) * mm, "end": v(133.68, -14.5) * mm});
            skPoint(sketch, "E181.oppositeSnap0", {"position": v(145, -12.9) * mm});
            skLineSegment(sketch, "E181.bottom", {"start": v(127.1, -6.75) * mm, "end": v(131.95, -6.75) * mm});
            skLineSegment(sketch, "E181.top", {"start": v(127.1, -12.9) * mm, "end": v(131.95, -12.9) * mm});
            skLineSegment(sketch, "E181.left", {"start": v(127.1, -6.75) * mm, "end": v(127.1, -12.9) * mm});
            skLineSegment(sketch, "E181.right", {"start": v(131.95, -6.75) * mm, "end": v(131.95, -12.9) * mm});
            skSolve(sketch);
        }
        {
            var Q0;
            Q0 = qSketchRegion(id + "F32", true);
            extrude(context, id + "F33", {"entities" : qUnion([Q0]), "operationType" : NewBodyOperationType.REMOVE, "oppositeDirection" : true, "depth" : 999 * mm});
        }
        {
            var Q0;
            Q0=makeQuery(id+"F9.opExtrude","SWEPT_FACE",FACE,{"disambiguationData":[OSD([sQuery(id+"F8.wireOp",EDGE,"E4.bottom")])]});
            var sketch = newSketch(context, id + "F34", { "sketchPlane" : qUnion([Q0])});
            skLineSegment(sketch, "E182.bottom", {"start": v(173.37, 0) * mm, "end": v(180.46, 0) * mm});
            skLineSegment(sketch, "E182.top", {"start": v(173.37, -5.81) * mm, "end": v(180.46, -5.81) * mm});
            skLineSegment(sketch, "E182.left", {"start": v(173.37, 0) * mm, "end": v(173.37, -5.81) * mm});
            skLineSegment(sketch, "E182.right", {"start": v(180.46, 0) * mm, "end": v(180.46, -5.81) * mm});
            skLineSegment(sketch, "E183.bottom", {"start": v(187.05, -7.95) * mm, "end": v(183.26, -7.95) * mm});
            skLineSegment(sketch, "E183.top", {"start": v(187.05, -13.16) * mm, "end": v(183.26, -13.16) * mm});
            skLineSegment(sketch, "E183.left", {"start": v(187.05, -7.95) * mm, "end": v(187.05, -13.16) * mm});
            skLineSegment(sketch, "E183.right", {"start": v(183.26, -7.95) * mm, "end": v(183.26, -13.16) * mm});
            skLineSegment(sketch, "E184.bottom", {"start": v(180.06, -20) * mm, "end": v(173.9, -20) * mm});
            skLineSegment(sketch, "E184.top", {"start": v(180.06, -14.5) * mm, "end": v(173.9, -14.5) * mm});
            skLineSegment(sketch, "E184.left", {"start": v(180.06, -20) * mm, "end": v(180.06, -14.5) * mm});
            skLineSegment(sketch, "E184.right", {"start": v(173.9, -20) * mm, "end": v(173.9, -14.5) * mm});
            skLineSegment(sketch, "E185.bottom", {"start": v(167.05, -8.08) * mm, "end": v(171.37, -8.08) * mm});
            skLineSegment(sketch, "E185.top", {"start": v(167.05, -13.43) * mm, "end": v(171.37, -13.43) * mm});
            skLineSegment(sketch, "E185.left", {"start": v(167.05, -8.08) * mm, "end": v(167.05, -13.43) * mm});
            skLineSegment(sketch, "E185.right", {"start": v(171.37, -8.08) * mm, "end": v(171.37, -13.43) * mm});
            skSolve(sketch);
        }
        {
            var Q0;
            Q0 = qSketchRegion(id + "F34", true);
            extrude(context, id + "F35", {"entities" : qUnion([Q0]), "operationType" : NewBodyOperationType.REMOVE, "oppositeDirection" : true, "depth" : 999 * mm});
        }
        {
            var Q0;
            Q0=makeQuery(id+"F7.opExtrude","SWEPT_FACE",FACE,{"disambiguationData":[OSD([sQuery(id+"F6.wireOp",EDGE,"E3.bottom")])]});
            var sketch = newSketch(context, id + "F36", { "sketchPlane" : qUnion([Q0])});
            skLineSegment(sketch, "E186.bottom", {"start": v(356.68, 0) * mm, "end": v(361.64, 0) * mm});
            skLineSegment(sketch, "E186.top", {"start": v(356.68, -3.9) * mm, "end": v(361.64, -3.9) * mm});
            skLineSegment(sketch, "E186.left", {"start": v(356.68, 0) * mm, "end": v(356.68, -3.9) * mm});
            skLineSegment(sketch, "E186.right", {"start": v(361.64, 0) * mm, "end": v(361.64, -3.9) * mm});
            skLineSegment(sketch, "E187.bottom", {"start": v(349.08, -7.82) * mm, "end": v(352.63, -7.82) * mm});
            skLineSegment(sketch, "E187.top", {"start": v(349.08, -12.66) * mm, "end": v(352.63, -12.66) * mm});
            skLineSegment(sketch, "E187.left", {"start": v(349.08, -7.82) * mm, "end": v(349.08, -12.66) * mm});
            skLineSegment(sketch, "E187.right", {"start": v(352.63, -7.82) * mm, "end": v(352.63, -12.66) * mm});
            skLineSegment(sketch, "E188.bottom", {"start": v(369.08, -7.82) * mm, "end": v(365.3, -7.82) * mm});
            skLineSegment(sketch, "E188.top", {"start": v(369.08, -12.66) * mm, "end": v(365.3, -12.66) * mm});
            skLineSegment(sketch, "E188.left", {"start": v(369.08, -7.82) * mm, "end": v(369.08, -12.66) * mm});
            skLineSegment(sketch, "E188.right", {"start": v(365.3, -7.82) * mm, "end": v(365.3, -12.66) * mm});
            skLineSegment(sketch, "E189.bottom", {"start": v(356.68, -40) * mm, "end": v(361.64, -40) * mm});
            skLineSegment(sketch, "E189.top", {"start": v(356.68, -35.91) * mm, "end": v(361.64, -35.91) * mm});
            skLineSegment(sketch, "E189.left", {"start": v(356.68, -40) * mm, "end": v(356.68, -35.91) * mm});
            skLineSegment(sketch, "E189.right", {"start": v(361.64, -40) * mm, "end": v(361.64, -35.91) * mm});
            skLineSegment(sketch, "E190", {"start": v(349.08, -20) * mm, "end": v(369.08, -20) * mm, "construction": true});
            skLineSegment(sketch, "E191.MirrorCS", {"start": v(369.08, -27.34) * mm, "end": v(365.3, -27.34) * mm});
            skLineSegment(sketch, "E192.MirrorCS", {"start": v(365.3, -32.18) * mm, "end": v(365.3, -27.34) * mm});
            skLineSegment(sketch, "E193.MirrorCS", {"start": v(369.08, -32.18) * mm, "end": v(369.08, -27.34) * mm});
            skLineSegment(sketch, "E194.MirrorCS", {"start": v(369.08, -32.18) * mm, "end": v(365.3, -32.18) * mm});
            skLineSegment(sketch, "E195.MirrorCS", {"start": v(352.63, -32.18) * mm, "end": v(352.63, -27.34) * mm});
            skLineSegment(sketch, "E196.MirrorCS", {"start": v(349.08, -32.18) * mm, "end": v(352.63, -32.18) * mm});
            skLineSegment(sketch, "E197.MirrorCS", {"start": v(349.08, -27.34) * mm, "end": v(352.63, -27.34) * mm});
            skLineSegment(sketch, "E198.MirrorCS", {"start": v(349.08, -32.18) * mm, "end": v(349.08, -27.34) * mm});
            skSolve(sketch);
        }
        {
            var Q0;
            Q0 = qSketchRegion(id + "F36", true);
            extrude(context, id + "F37", {"entities" : qUnion([Q0]), "operationType" : NewBodyOperationType.REMOVE, "oppositeDirection" : true, "depth" : 999 * mm});
        }
        {
            var Q0;
            Q0=makeQuery(id+"F21.opExtrude","SWEPT_FACE",FACE,{"disambiguationData":[OSD([sQuery(id+"F20.wireOp",EDGE,"E10.bottom")])]});
            var sketch = newSketch(context, id + "F38", { "sketchPlane" : qUnion([Q0])});
            skLineSegment(sketch, "E199.bottom", {"start": v(433.52, 0) * mm, "end": v(440.17, 0) * mm});
            skLineSegment(sketch, "E199.top", {"start": v(433.52, -4.33) * mm, "end": v(440.17, -4.33) * mm});
            skLineSegment(sketch, "E199.left", {"start": v(433.52, 0) * mm, "end": v(433.52, -4.33) * mm});
            skLineSegment(sketch, "E199.right", {"start": v(440.17, 0) * mm, "end": v(440.17, -4.33) * mm});
            skLineSegment(sketch, "E200.bottom", {"start": v(446.75, -6.62) * mm, "end": v(443.08, -6.62) * mm});
            skLineSegment(sketch, "E200.top", {"start": v(446.75, -13.47) * mm, "end": v(443.08, -13.47) * mm});
            skLineSegment(sketch, "E200.left", {"start": v(446.75, -6.62) * mm, "end": v(446.75, -13.47) * mm});
            skLineSegment(sketch, "E200.right", {"start": v(443.08, -6.62) * mm, "end": v(443.08, -13.47) * mm});
            skLineSegment(sketch, "E201.bottom", {"start": v(426.75, -6.62) * mm, "end": v(431.44, -6.62) * mm});
            skLineSegment(sketch, "E201.top", {"start": v(426.75, -13.47) * mm, "end": v(431.44, -13.47) * mm});
            skLineSegment(sketch, "E201.left", {"start": v(426.75, -6.62) * mm, "end": v(426.75, -13.47) * mm});
            skLineSegment(sketch, "E201.right", {"start": v(431.44, -6.62) * mm, "end": v(431.44, -13.47) * mm});
            skLineSegment(sketch, "E202", {"start": v(426.75, -20) * mm, "end": v(446.75, -20) * mm, "construction": true});
            skLineSegment(sketch, "E203.MirrorCS", {"start": v(426.75, -33.38) * mm, "end": v(431.44, -33.38) * mm});
            skLineSegment(sketch, "E204.MirrorCS", {"start": v(426.75, -26.53) * mm, "end": v(431.44, -26.53) * mm});
            skLineSegment(sketch, "E205.MirrorCS", {"start": v(433.52, -40) * mm, "end": v(433.52, -35.67) * mm});
            skLineSegment(sketch, "E206.MirrorCS", {"start": v(446.75, -26.53) * mm, "end": v(443.08, -26.53) * mm});
            skLineSegment(sketch, "E207.MirrorCS", {"start": v(440.17, -40) * mm, "end": v(440.17, -35.67) * mm});
            skLineSegment(sketch, "E208.MirrorCS", {"start": v(446.75, -33.38) * mm, "end": v(443.08, -33.38) * mm});
            skLineSegment(sketch, "E209.MirrorCS", {"start": v(433.52, -40) * mm, "end": v(440.17, -40) * mm});
            skLineSegment(sketch, "E210.MirrorCS", {"start": v(433.52, -35.67) * mm, "end": v(440.17, -35.67) * mm});
            skLineSegment(sketch, "E211.MirrorCS", {"start": v(443.08, -33.38) * mm, "end": v(443.08, -26.53) * mm});
            skLineSegment(sketch, "E212.MirrorCS", {"start": v(446.75, -33.38) * mm, "end": v(446.75, -26.53) * mm});
            skLineSegment(sketch, "E213.MirrorCS", {"start": v(431.44, -33.38) * mm, "end": v(431.44, -26.53) * mm});
            skLineSegment(sketch, "E214.MirrorCS", {"start": v(426.75, -33.38) * mm, "end": v(426.75, -26.53) * mm});
            skSolve(sketch);
        }
        {
            var Q0;
            Q0 = qSketchRegion(id + "F38", true);
            extrude(context, id + "F39", {"entities" : qUnion([Q0]), "operationType" : NewBodyOperationType.REMOVE, "oppositeDirection" : true, "depth" : 999 * mm});
        }
        {
            var Q0;
            Q0=qCreatedBy(makeId("Front.planeOp"),FACE);
            var sketch = newSketch(context, id + "F40", { "sketchPlane" : qUnion([Q0])});
            skLineSegment(sketch, "E215.bottom", {"start": v(-98.07, -89.41) * mm, "end": v(-78.07, -89.41) * mm});
            skLineSegment(sketch, "E215.top", {"start": v(-98.07, -149.41) * mm, "end": v(-38.07, -149.41) * mm});
            skLineSegment(sketch, "E215.left", {"start": v(-98.07, -89.41) * mm, "end": v(-98.07, -149.41) * mm});
            skLineSegment(sketch, "E215.right", {"start": v(-38.07, -129.41) * mm, "end": v(-38.07, -149.41) * mm});
            skLineSegment(sketch, "E216.top", {"start": v(-98.07, -149.41) * mm, "end": v(-78.07, -149.41) * mm});
            skLineSegment(sketch, "E217.right", {"start": v(-38.07, -149.41) * mm, "end": v(-38.07, -129.41) * mm});
            skLineSegment(sketch, "E218", {"start": v(-78.07, -89.41) * mm, "end": v(-38.07, -129.41) * mm});
            skLineSegment(sketch, "E219", {"start": v(-98.07, -139.41) * mm, "end": v(-38.07, -139.41) * mm, "construction": true});
            skCircle(sketch, "E220", {"center": v(-88.07, -139.41) * mm, "radius": 2.6 * mm});
            skCircle(sketch, "E221.MirrorC", {"center": v(-88.07, -119.41) * mm, "radius": 2.6 * mm});
            skCircle(sketch, "E222.MirrorC", {"center": v(-68.07, -139.41) * mm, "radius": 2.6 * mm});
            skLineSegment(sketch, "E223.bottom", {"start": v(-98.07, -89.41) * mm, "end": v(-78.07, -89.41) * mm, "construction": true});
            skLineSegment(sketch, "E223.left", {"start": v(-98.07, -89.41) * mm, "end": v(-98.07, -129.41) * mm, "construction": true});
            skCircle(sketch, "E224.MirrorC", {"center": v(-48.07, -139.41) * mm, "radius": 2.6 * mm});
            skCircle(sketch, "E225.MirrorC", {"center": v(-88.07, -99.41) * mm, "radius": 2.6 * mm});
            skSolve(sketch);
        }
        {
            var Q0;
            Q0 = qSketchRegion(id + "F40", true);
            extrude(context, id + "F41", {"entities" : qUnion([Q0]), "depth" : 3.5 * mm});
        }
        {
            var Q0;
            Q0=qCreatedBy(makeId("Front.planeOp"),FACE);
            var sketch = newSketch(context, id + "F42", { "sketchPlane" : qUnion([Q0])});
            skLineSegment(sketch, "E226.bottom", {"start": v(-263.76, -84.08) * mm, "end": v(-243.76, -84.08) * mm});
            skLineSegment(sketch, "E226.top", {"start": v(-263.76, -144.08) * mm, "end": v(-203.76, -144.08) * mm});
            skLineSegment(sketch, "E226.right", {"start": v(-203.76, -124.08) * mm, "end": v(-203.76, -144.08) * mm});
            skLineSegment(sketch, "E227.right", {"start": v(-203.76, -144.08) * mm, "end": v(-203.76, -124.08) * mm});
            skLineSegment(sketch, "E228", {"start": v(-243.76, -84.08) * mm, "end": v(-203.76, -124.08) * mm});
            skCircle(sketch, "E229", {"center": v(-253.76, -134.08) * mm, "radius": 2.6 * mm});
            skCircle(sketch, "E230.MirrorC", {"center": v(-253.76, -114.08) * mm, "radius": 2.6 * mm});
            skCircle(sketch, "E231.MirrorC", {"center": v(-233.76, -134.08) * mm, "radius": 2.6 * mm});
            skCircle(sketch, "E232.MirrorC", {"center": v(-213.76, -134.08) * mm, "radius": 2.6 * mm});
            skCircle(sketch, "E233.MirrorC", {"center": v(-253.76, -94.08) * mm, "radius": 2.6 * mm});
            skLineSegment(sketch, "E234.MirrorCS", {"start": v(-263.76, -84.08) * mm, "end": v(-303.76, -124.08) * mm});
            skCircle(sketch, "E235.MirrorC", {"center": v(-273.76, -134.08) * mm, "radius": 2.6 * mm});
            skCircle(sketch, "E236.MirrorC", {"center": v(-293.76, -134.08) * mm, "radius": 2.6 * mm});
            skLineSegment(sketch, "E237", {"start": v(-263.76, -144.08) * mm, "end": v(-303.76, -144.08) * mm});
            skLineSegment(sketch, "E238", {"start": v(-303.76, -124.08) * mm, "end": v(-303.76, -144.08) * mm});
            skPoint(sketch, "E239.orphan", {"position": v(-243.76, -104.08) * mm});
            skPoint(sketch, "E240.start.orphan", {"position": v(-263.76, -104.08) * mm});
            skSolve(sketch);
        }
        {
            var Q0;
            Q0 = qSketchRegion(id + "F42", true);
            extrude(context, id + "F43", {"entities" : qUnion([Q0]), "depth" : 3.5 * mm});
        }
    });
